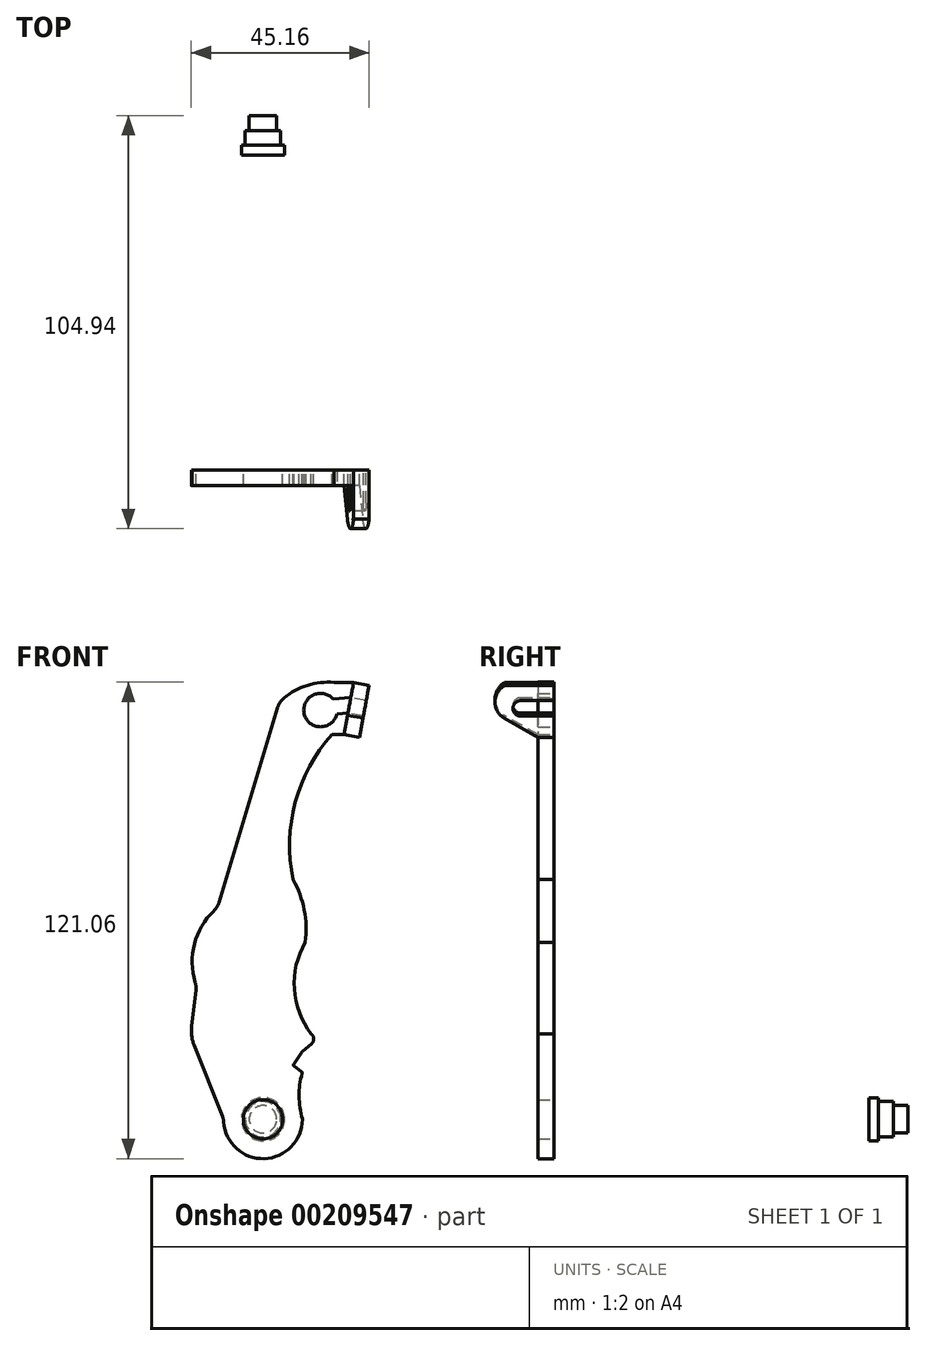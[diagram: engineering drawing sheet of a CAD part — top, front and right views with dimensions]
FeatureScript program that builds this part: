
annotation { "Feature Type Name" : "Feature", "Feature Type Description" : "" }
export const myFeature = defineFeature(function(context is Context, id is Id, definition is map)
    precondition{}
    {
        {
            var Q0;
            Q0=qCreatedBy(makeId("Front.planeOp"),FACE);
            var sketch = newSketch(context, id + "F0", { "sketchPlane" : qUnion([Q0])});
            skCircle(sketch, "E0", {"center": v(0, 0) * mm, "radius": 5 * mm});
            skArc(sketch, "E1", {"start": v(1.74, 9.85) * mm, "mid": v(0.87, 9.96) * mm, "end": v(0, 10) * mm, "construction": true});
            skLineSegment(sketch, "E2", {"start": v(0, 0) * mm, "end": v(28.93, 34.47) * mm, "construction": true});
            skLineSegment(sketch, "E3", {"start": v(0, 0) * mm, "end": v(48.75, 69.63) * mm, "construction": true});
            skLineSegment(sketch, "E4", {"start": v(0, 0) * mm, "end": v(0, 40) * mm, "construction": true});
            skLineSegment(sketch, "E5", {"start": v(0, 0) * mm, "end": v(16.5, 93.56) * mm, "construction": true});
            skArc(sketch, "E6", {"start": v(10.74, 44.97) * mm, "mid": v(7.97, 33.1) * mm, "end": v(12.27, 21.69) * mm});
            skArc(sketch, "E7", {"start": v(17.54, 97.73) * mm, "mid": v(8.19, 80.5) * mm, "end": v(7.67, 60.9) * mm});
            skLineSegment(sketch, "E8", {"start": v(48.75, 69.63) * mm, "end": v(17.54, 97.73) * mm, "construction": true});
            skLineSegment(sketch, "E9", {"start": v(48.75, 69.63) * mm, "end": v(7.67, 60.9) * mm, "construction": true});
            skLineSegment(sketch, "E10", {"start": v(28.93, 34.47) * mm, "end": v(12.27, 21.69) * mm, "construction": true});
            skLineSegment(sketch, "E11", {"start": v(28.93, 34.47) * mm, "end": v(10.74, 44.97) * mm, "construction": true});
            skArc(sketch, "E12", {"start": v(10.74, 44.97) * mm, "mid": v(10.48, 53.18) * mm, "end": v(7.67, 60.9) * mm});
            skLineSegment(sketch, "E13", {"start": v(0, 0) * mm, "end": v(10, 0) * mm, "construction": true});
            skArc(sketch, "E14.trimOffspring", {"start": v(-9.98, -0.7) * mm, "mid": v(0.31, -10) * mm, "end": v(10, -0.07) * mm});
            skArc(sketch, "E15", {"start": v(18.02, 111) * mm, "mid": v(11.28, 110.26) * mm, "end": v(5.32, 107.02) * mm});
            skLineSegment(sketch, "E16", {"start": v(16.5, 93.56) * mm, "end": v(18.02, 111) * mm, "construction": true});
            skLineSegment(sketch, "E17", {"start": v(16.5, 93.56) * mm, "end": v(4.12, 105.93) * mm, "construction": true});
            skArc(sketch, "E18", {"start": v(-12.49, 52.96) * mm, "mid": v(-17.42, 44.54) * mm, "end": v(-17.23, 34.78) * mm});
            skLineSegment(sketch, "E19", {"start": v(0, 40) * mm, "end": v(-11.57, 53.79) * mm, "construction": true});
            skLineSegment(sketch, "E20", {"start": v(0, 40) * mm, "end": v(-16.91, 33.84) * mm, "construction": true});
            skArc(sketch, "E21.trimOffspring", {"start": v(10.08, 54.91) * mm, "mid": v(9.9, 55.03) * mm, "end": v(9.72, 55.15) * mm});
            skLineSegment(sketch, "E22", {"start": v(0, 0) * mm, "end": v(-8.2, 22.55) * mm, "construction": true});
            skArc(sketch, "E23", {"start": v(-18.14, 23.75) * mm, "mid": v(-18.13, 21.27) * mm, "end": v(-17.5, 18.86) * mm});
            skLineSegment(sketch, "E24", {"start": v(-10.32, 0.8) * mm, "end": v(-17.5, 18.86) * mm});
            skLineSegment(sketch, "E25", {"start": v(-17.05, 32.73) * mm, "end": v(-18.14, 23.75) * mm});
            skLineSegment(sketch, "E26", {"start": v(3.73, 104.62) * mm, "end": v(-11.17, 55.12) * mm});
            skPoint(sketch, "E27.visualSharp", {"position": v(4.12, 105.93) * mm});
            skArc(sketch, "E27.filletArc", {"start": v(5.32, 107.02) * mm, "mid": v(4.35, 105.94) * mm, "end": v(3.73, 104.62) * mm});
            skPoint(sketch, "E28.visualSharp", {"position": v(-11.57, 53.79) * mm});
            skArc(sketch, "E28.filletArc", {"start": v(-12.49, 52.96) * mm, "mid": v(-11.69, 53.96) * mm, "end": v(-11.17, 55.12) * mm});
            skPoint(sketch, "E29.visualSharp", {"position": v(-16.91, 33.84) * mm});
            skArc(sketch, "E29.filletArc", {"start": v(-17.05, 32.73) * mm, "mid": v(-17.03, 33.77) * mm, "end": v(-17.23, 34.78) * mm});
            skPoint(sketch, "E30.visualSharp", {"position": v(-10, 0) * mm});
            skArc(sketch, "E30.filletArc", {"start": v(-9.98, -0.7) * mm, "mid": v(-10.09, 0.06) * mm, "end": v(-10.32, 0.8) * mm});
            skPoint(sketch, "E31", {"position": v(10, 12) * mm});
            skArc(sketch, "E32", {"start": v(9.9, 11.66) * mm, "mid": v(9.17, 5.86) * mm, "end": v(9.98, 0.07) * mm});
            skLineSegment(sketch, "E33", {"start": v(9.71, 12.2) * mm, "end": v(7.95, 13.43) * mm});
            skLineSegment(sketch, "E34", {"start": v(7.83, 14.13) * mm, "end": v(9.92, 17.12) * mm});
            skLineSegment(sketch, "E35", {"start": v(10.1, 17.31) * mm, "end": v(12.3, 19.16) * mm});
            skArc(sketch, "E36", {"start": v(12.3, 19.16) * mm, "mid": v(12.88, 20.43) * mm, "end": v(12.27, 21.69) * mm});
            skPoint(sketch, "E37.visualSharp", {"position": v(7.54, 13.72) * mm});
            skArc(sketch, "E37.filletArc", {"start": v(7.83, 14.13) * mm, "mid": v(7.75, 13.76) * mm, "end": v(7.95, 13.43) * mm});
            skPoint(sketch, "E38.visualSharp", {"position": v(10, 17.23) * mm});
            skArc(sketch, "E38.filletArc", {"start": v(10.1, 17.31) * mm, "mid": v(10, 17.22) * mm, "end": v(9.92, 17.12) * mm});
            skArc(sketch, "E39.filletArc", {"start": v(9.9, 11.66) * mm, "mid": v(9.9, 11.96) * mm, "end": v(9.71, 12.2) * mm});
            skPoint(sketch, "E40.visualSharp", {"position": v(10, 0) * mm});
            skArc(sketch, "E40.filletArc", {"start": v(10, -0.07) * mm, "mid": v(10, 0) * mm, "end": v(9.98, 0.07) * mm});
            skLineSegment(sketch, "E41", {"start": v(0, 0) * mm, "end": v(14.61, 103.98) * mm, "construction": true});
            skCircle(sketch, "E42", {"center": v(14.61, 103.98) * mm, "radius": 4.25 * mm});
            skLineSegment(sketch, "E43", {"start": v(18.02, 111) * mm, "end": v(23.02, 111) * mm});
            skLineSegment(sketch, "E44", {"start": v(17.54, 97.73) * mm, "end": v(20.54, 97.73) * mm});
            skLineSegment(sketch, "E45", {"start": v(23.02, 111) * mm, "end": v(20.54, 97.73) * mm});
            skSolve(sketch);
        }
        {
            var Q0;
            Q0=makeQuery(id+"F0.imprint","IMPRINT",FACE,{"disambiguationData":[TD([[makeQuery(id+"F0.imprint","IMPRINT",EDGE,{"derivedFrom":sQuery(id+"F0.wireOp",EDGE,"E0")}),-1.0]])]});
            extrude(context, id + "F1", {"entities" : qUnion([Q0]), "depth" : 4 * mm});
        }
        {
            var Q0;
            Q0=makeQuery(id+"F1.opExtrude","SWEPT_FACE",FACE,{"disambiguationData":[OSD([sQuery(id+"F0.wireOp",EDGE,"E45")])]});
            var sketch = newSketch(context, id + "F2", { "sketchPlane" : qUnion([Q0])});
            skLineSegment(sketch, "E46.0", {"start": v(-4, 99.84) * mm, "end": v(0, 99.84) * mm});
            skLineSegment(sketch, "E47.0", {"start": v(-4, 113.33) * mm, "end": v(0, 113.33) * mm});
            skLineSegment(sketch, "E48", {"start": v(-4, 99.84) * mm, "end": v(-12.66, 104.84) * mm});
            skLineSegment(sketch, "E49", {"start": v(-4, 113.33) * mm, "end": v(-12.5, 113.33) * mm});
            skArc(sketch, "E50", {"start": v(-12.5, 113.33) * mm, "mid": v(-14.94, 109.13) * mm, "end": v(-12.66, 104.84) * mm});
            skPoint(sketch, "E51.startSnap0", {"position": v(-14.94, 109.13) * mm});
            skArc(sketch, "E52", {"start": v(-8.4, 109.38) * mm, "mid": v(-10.4, 107.38) * mm, "end": v(-8.4, 105.38) * mm});
            skLineSegment(sketch, "E53", {"start": v(-8.4, 105.38) * mm, "end": v(0, 105.38) * mm});
            skLineSegment(sketch, "E54", {"start": v(-8.4, 109.38) * mm, "end": v(0, 109.38) * mm});
            skLineSegment(sketch, "E55", {"start": v(-8.4, 107.38) * mm, "end": v(-8.4, 102.38) * mm, "construction": true});
            skLineSegment(sketch, "E56", {"start": v(-8.4, 107.38) * mm, "end": v(0, 107.38) * mm, "construction": true});
            skLineSegment(sketch, "E57", {"start": v(0, 99.84) * mm, "end": v(0, 105.38) * mm});
            skLineSegment(sketch, "E58", {"start": v(0, 109.38) * mm, "end": v(0, 113.33) * mm});
            skSolve(sketch);
        }
        {
            var Q0;
            Q0 = qSketchRegion(id + "F2", true);
            extrude(context, id + "F3", {"entities" : qUnion([Q0]), "operationType" : NewBodyOperationType.ADD, "depth" : 4 * mm});
        }
        {
            var Q0;
            Q0=makeQuery(id+"F1.opExtrude","CAP_FACE",FACE,{"disambiguationData":[OSD([sQuery(id+"F0.wireOp",EDGE,"E0"),sQuery(id+"F0.wireOp",EDGE,"E6"),sQuery(id+"F0.wireOp",EDGE,"E7"),sQuery(id+"F0.wireOp",EDGE,"E12"),sQuery(id+"F0.wireOp",EDGE,"E14.trimOffspring"),sQuery(id+"F0.wireOp",EDGE,"E15"),sQuery(id+"F0.wireOp",EDGE,"E18"),sQuery(id+"F0.wireOp",EDGE,"E23"),sQuery(id+"F0.wireOp",EDGE,"E24"),sQuery(id+"F0.wireOp",EDGE,"E25"),sQuery(id+"F0.wireOp",EDGE,"E26"),sQuery(id+"F0.wireOp",EDGE,"E27.filletArc"),sQuery(id+"F0.wireOp",EDGE,"E28.filletArc"),sQuery(id+"F0.wireOp",EDGE,"E29.filletArc"),sQuery(id+"F0.wireOp",EDGE,"E30.filletArc"),sQuery(id+"F0.wireOp",EDGE,"E32"),sQuery(id+"F0.wireOp",EDGE,"E33"),sQuery(id+"F0.wireOp",EDGE,"E34"),sQuery(id+"F0.wireOp",EDGE,"E35"),sQuery(id+"F0.wireOp",EDGE,"E36"),sQuery(id+"F0.wireOp",EDGE,"E37.filletArc"),sQuery(id+"F0.wireOp",EDGE,"E38.filletArc"),sQuery(id+"F0.wireOp",EDGE,"E39.filletArc"),sQuery(id+"F0.wireOp",EDGE,"E40.filletArc"),sQuery(id+"F0.wireOp",EDGE,"E42"),sQuery(id+"F0.wireOp",EDGE,"E43"),sQuery(id+"F0.wireOp",EDGE,"E44"),sQuery(id+"F0.wireOp",EDGE,"E45")])],"isStart":false});
            var sketch = newSketch(context, id + "F4", { "sketchPlane" : qUnion([Q0])});
            skCircle(sketch, "E59.0", {"center": v(14.61, 103.98) * mm, "radius": 4.25 * mm});
            skLineSegment(sketch, "E60.0", {"start": v(22.3, 107.1) * mm, "end": v(21.56, 103.18) * mm});
            skLineSegment(sketch, "E61", {"start": v(21.56, 103.18) * mm, "end": v(18.75, 103) * mm});
            skLineSegment(sketch, "E62", {"start": v(22.3, 107.1) * mm, "end": v(17.78, 106.8) * mm});
            skSolve(sketch);
        }
        {
            var Q0;
            Q0 = qSketchRegion(id + "F4", true);
            extrude(context, id + "F5", {"entities" : qUnion([Q0]), "operationType" : NewBodyOperationType.REMOVE, "oppositeDirection" : true, "depth" : 25 * mm});
        }
        {
            var Q0;
            Q0=qCreatedBy(makeId("Right.planeOp"),FACE);
            var sketch = newSketch(context, id + "F6", { "sketchPlane" : qUnion([Q0])});
            skLineSegment(sketch, "E63", {"start": v(0, 0) * mm, "end": v(80, 0) * mm, "construction": true});
            skLineSegment(sketch, "E64", {"start": v(80, 0) * mm, "end": v(80, 5.5) * mm});
            skLineSegment(sketch, "E65", {"start": v(80, 5.5) * mm, "end": v(82.5, 5.5) * mm});
            skLineSegment(sketch, "E66", {"start": v(80, 0) * mm, "end": v(90, 0) * mm});
            skLineSegment(sketch, "E67", {"start": v(90, 0) * mm, "end": v(90, 3.5) * mm});
            skLineSegment(sketch, "E68", {"start": v(90, 3.5) * mm, "end": v(86.25, 3.5) * mm});
            skLineSegment(sketch, "E69", {"start": v(86.25, 3.5) * mm, "end": v(86.25, 4.5) * mm});
            skLineSegment(sketch, "E70", {"start": v(86.25, 4.5) * mm, "end": v(82.5, 4.5) * mm});
            skLineSegment(sketch, "E71", {"start": v(82.5, 4.5) * mm, "end": v(82.5, 5.5) * mm});
            skSolve(sketch);
        }
        {
            var Q0;
            Q0=makeQuery(id+"F6.imprint","IMPRINT",FACE,{"disambiguationData":[TD([[makeQuery(id+"F6.imprint","IMPRINT",EDGE,{"derivedFrom":sQuery(id+"F6.wireOp",EDGE,"E64")}),-1.0]])]});
            var Q1;
            Q1=sQuery(id+"F6.wireOp",EDGE,"E66");
            revolve(context, id + "F7", {"entities" : qUnion([Q0]), "axis" : qUnion([Q1]), "revolveType" : RevolveType.FULL});
        }
    });
